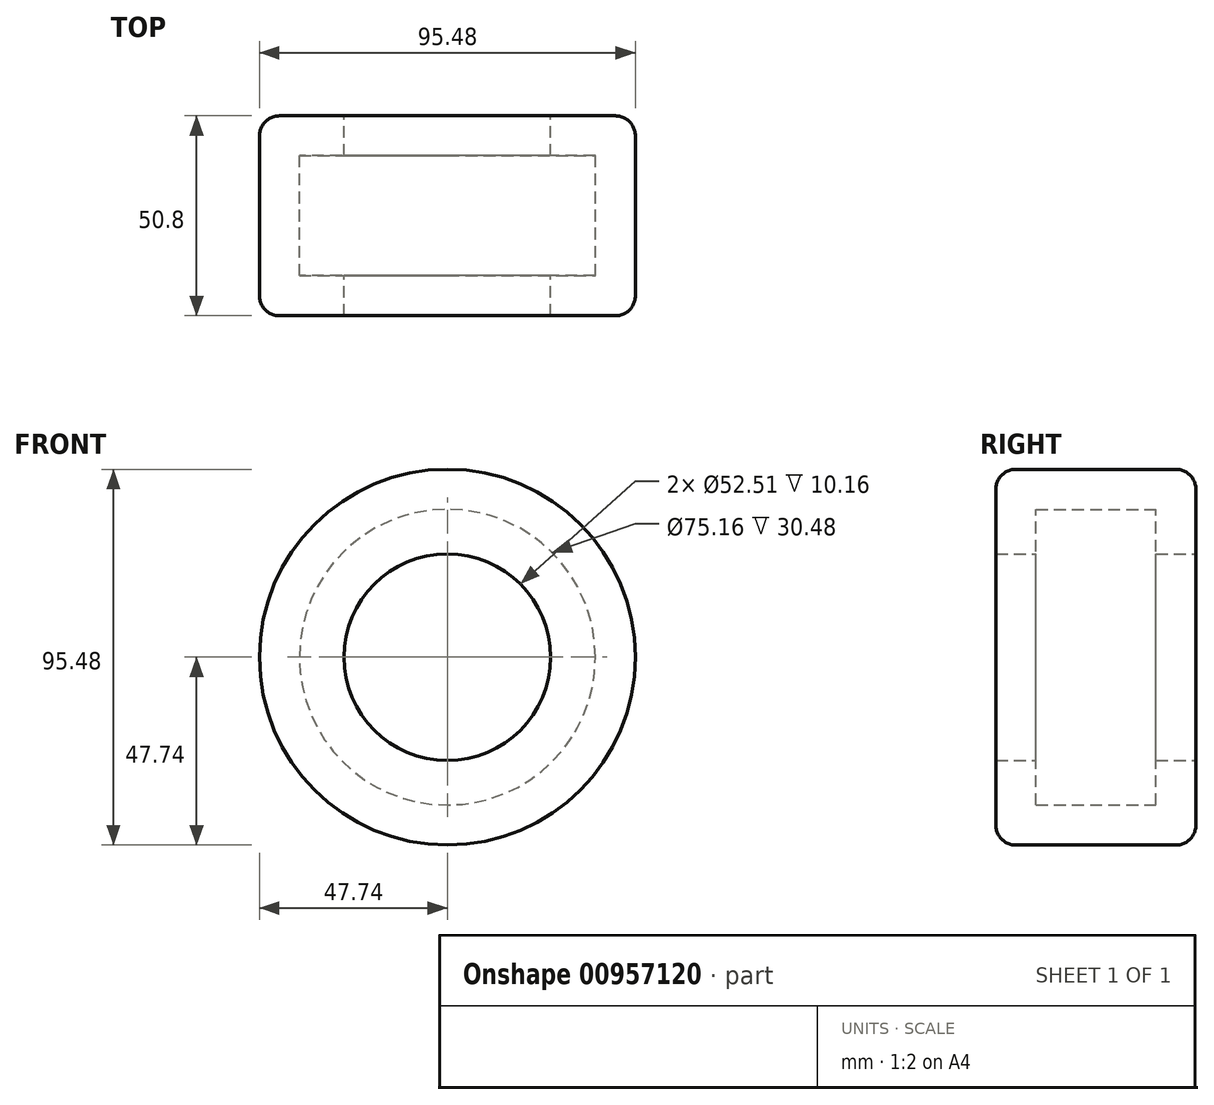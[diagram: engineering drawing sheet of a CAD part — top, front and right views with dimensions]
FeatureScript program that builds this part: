
annotation { "Feature Type Name" : "Feature", "Feature Type Description" : "" }
export const myFeature = defineFeature(function(context is Context, id is Id, definition is map)
    precondition{}
    {
        {
            var Q0;
            Q0=qCreatedBy(makeId("Front.planeOp"),FACE);
            var sketch = newSketch(context, id + "F0", { "sketchPlane" : qUnion([Q0])});
            skCircle(sketch, "E0", {"center": v(0, 0) * mm, "radius": 47.74 * mm});
            skCircle(sketch, "E1", {"center": v(0, 0) * mm, "radius": 26.25 * mm});
            skSolve(sketch);
        }
        {
            var Q0;
            Q0=makeQuery(id+"F0.imprint","IMPRINT",FACE,{"disambiguationData":[TD([[makeQuery(id+"F0.imprint","IMPRINT",EDGE,{"derivedFrom":sQuery(id+"F0.wireOp",EDGE,"E0")}),1.0]])]});
            extrude(context, id + "F1", {"entities" : qUnion([Q0]), "endBound" : BoundingType.SYMMETRIC, "depth" : 50.8 * mm, "offsetDistance" : 25.4 * mm});
        }
        {
            var Q0;
            Q0=makeQuery(id+"F1.opExtrude","CAP_EDGE",EDGE,{"disambiguationData":[OSD([sQuery(id+"F0.wireOp",EDGE,"E0")])],"isStart":false});
            fillet(context, id + "F2", {"entities" : qUnion([Q0]), "radius" : 5.08 * mm, "tangentPropagation" : true, "allowEdgeOverflow" : false});
        }
        {
            var Q0;
            Q0=makeQuery(id+"F1.opExtrude","CAP_EDGE",EDGE,{"disambiguationData":[OSD([sQuery(id+"F0.wireOp",EDGE,"E0")])],"isStart":true});
            fillet(context, id + "F3", {"entities" : qUnion([Q0]), "radius" : 5.08 * mm, "tangentPropagation" : true, "allowEdgeOverflow" : false});
        }
        {
            var Q0;
            Q0=makeQuery(id+"F1.opExtrude","SWEPT_FACE",FACE,{"disambiguationData":[OSD([sQuery(id+"F0.wireOp",EDGE,"E1")])]});
            shell(context, id + "F4", {"entities" : qUnion([Q0]), "thickness" : 10.16 * mm});
        }
    });
